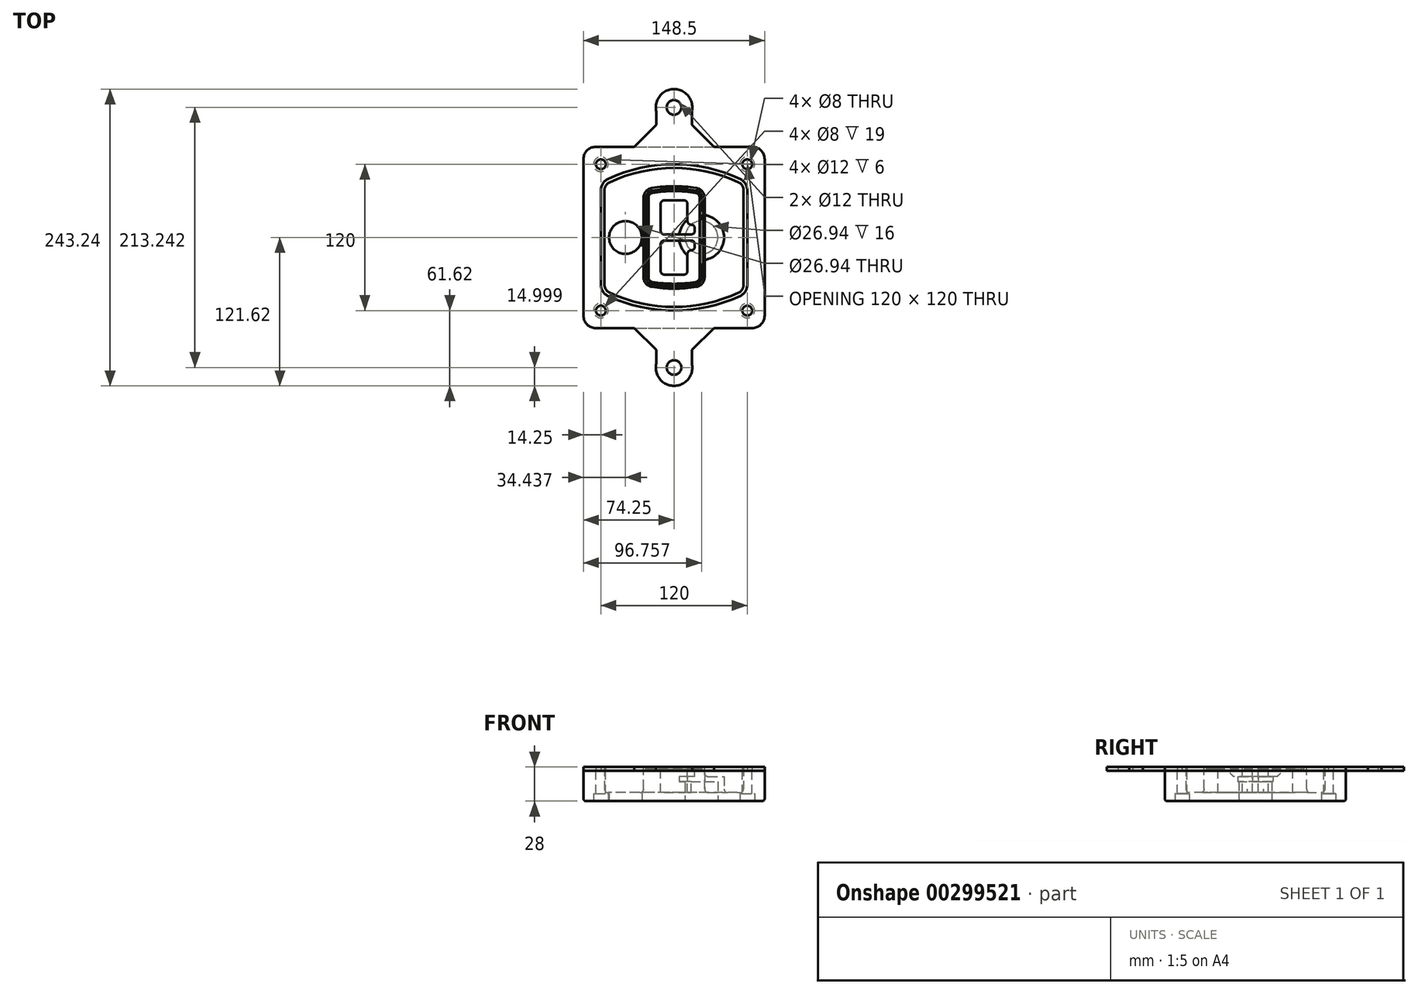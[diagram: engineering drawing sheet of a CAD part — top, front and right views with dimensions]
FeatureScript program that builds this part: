
annotation { "Feature Type Name" : "Feature", "Feature Type Description" : "" }
export const myFeature = defineFeature(function(context is Context, id is Id, definition is map)
    precondition{}
    {
        {
            var Q0;
            Q0=qCreatedBy(makeId("Top.planeOp"),FACE);
            var sketch = newSketch(context, id + "F0", { "sketchPlane" : qUnion([Q0])});
            skPoint(sketch, "E0.rect.middle", {"position": v(0, 0) * mm});
            skLineSegment(sketch, "E1.bottom", {"start": v(-64.25, -74.25) * mm, "end": v(64.25, -74.25) * mm});
            skLineSegment(sketch, "E1.top", {"start": v(-64.25, 74.25) * mm, "end": v(64.25, 74.25) * mm});
            skLineSegment(sketch, "E1.left", {"start": v(-74.25, -64.25) * mm, "end": v(-74.25, 64.25) * mm});
            skLineSegment(sketch, "E1.right", {"start": v(74.25, -64.25) * mm, "end": v(74.25, 64.25) * mm});
            skLineSegment(sketch, "E2", {"start": v(-74.25, 74.25) * mm, "end": v(74.25, -74.25) * mm, "construction": true});
            skLineSegment(sketch, "E3", {"start": v(74.25, 74.25) * mm, "end": v(-74.25, -74.25) * mm, "construction": true});
            skCircle(sketch, "E4", {"center": v(-60, 60) * mm, "radius": 4 * mm});
            skCircle(sketch, "E5", {"center": v(60, 60) * mm, "radius": 4 * mm});
            skCircle(sketch, "E6", {"center": v(60, -60) * mm, "radius": 4 * mm});
            skCircle(sketch, "E7", {"center": v(-60, -60) * mm, "radius": 4 * mm});
            skLineSegment(sketch, "E8", {"start": v(-60, 60) * mm, "end": v(60, 60) * mm, "construction": true});
            skLineSegment(sketch, "E9", {"start": v(60, 60) * mm, "end": v(60, -60) * mm, "construction": true});
            skLineSegment(sketch, "E10", {"start": v(60, -60) * mm, "end": v(-60, -60) * mm, "construction": true});
            skLineSegment(sketch, "E11", {"start": v(-60, -60) * mm, "end": v(-60, 60) * mm, "construction": true});
            skLineSegment(sketch, "E12", {"start": v(-60, 38.83) * mm, "end": v(-60, -38.83) * mm});
            skLineSegment(sketch, "E13", {"start": v(60, 38.83) * mm, "end": v(60, -38.83) * mm});
            skArc(sketch, "E14", {"start": v(54.26, 47.88) * mm, "mid": v(0, 60) * mm, "end": v(-54.26, 47.88) * mm});
            skArc(sketch, "E15", {"start": v(-54.26, -47.88) * mm, "mid": v(0, -60) * mm, "end": v(54.26, -47.88) * mm});
            skLineSegment(sketch, "E16", {"start": v(-60, 0) * mm, "end": v(60, 0) * mm, "construction": true});
            skPoint(sketch, "E17.visualSharp", {"position": v(-60, -45) * mm});
            skArc(sketch, "E17.filletArc", {"start": v(-60, -38.83) * mm, "mid": v(-58.44, -44.2) * mm, "end": v(-54.26, -47.88) * mm});
            skPoint(sketch, "E18.visualSharp", {"position": v(-60, 45) * mm});
            skArc(sketch, "E18.filletArc", {"start": v(-54.26, 47.88) * mm, "mid": v(-58.44, 44.2) * mm, "end": v(-60, 38.83) * mm});
            skPoint(sketch, "E19.visualSharp", {"position": v(60, 45) * mm});
            skArc(sketch, "E19.filletArc", {"start": v(60, 38.83) * mm, "mid": v(58.44, 44.2) * mm, "end": v(54.26, 47.88) * mm});
            skPoint(sketch, "E20.visualSharp", {"position": v(60, -45) * mm});
            skArc(sketch, "E20.filletArc", {"start": v(54.26, -47.88) * mm, "mid": v(58.44, -44.2) * mm, "end": v(60, -38.83) * mm});
            skPoint(sketch, "E21.visualSharp", {"position": v(-74.25, 74.25) * mm});
            skArc(sketch, "E21.filletArc", {"start": v(-64.25, 74.25) * mm, "mid": v(-71.32, 71.32) * mm, "end": v(-74.25, 64.25) * mm});
            skPoint(sketch, "E22.visualSharp", {"position": v(74.25, 74.25) * mm});
            skArc(sketch, "E22.filletArc", {"start": v(74.25, 64.25) * mm, "mid": v(71.32, 71.32) * mm, "end": v(64.25, 74.25) * mm});
            skPoint(sketch, "E23.visualSharp", {"position": v(74.25, -74.25) * mm});
            skArc(sketch, "E23.filletArc", {"start": v(64.25, -74.25) * mm, "mid": v(71.32, -71.32) * mm, "end": v(74.25, -64.25) * mm});
            skPoint(sketch, "E24.visualSharp", {"position": v(-74.25, -74.25) * mm});
            skArc(sketch, "E24.filletArc", {"start": v(-74.25, -64.25) * mm, "mid": v(-71.32, -71.32) * mm, "end": v(-64.25, -74.25) * mm});
            skArc(sketch, "E25.0", {"start": v(57, 38.83) * mm, "mid": v(55.9, 42.58) * mm, "end": v(52.98, 45.17) * mm});
            skLineSegment(sketch, "E25.1", {"start": v(57, 38.83) * mm, "end": v(57, -38.83) * mm});
            skArc(sketch, "E25.2", {"start": v(52.98, -45.17) * mm, "mid": v(55.9, -42.58) * mm, "end": v(57, -38.83) * mm});
            skArc(sketch, "E25.3", {"start": v(-52.98, -45.17) * mm, "mid": v(0, -57) * mm, "end": v(52.98, -45.17) * mm});
            skArc(sketch, "E25.4", {"start": v(-57, -38.83) * mm, "mid": v(-55.9, -42.58) * mm, "end": v(-52.98, -45.17) * mm});
            skArc(sketch, "E25.5", {"start": v(52.98, 45.17) * mm, "mid": v(0, 57) * mm, "end": v(-52.98, 45.17) * mm});
            skLineSegment(sketch, "E25.6", {"start": v(-57, 38.83) * mm, "end": v(-57, -38.83) * mm});
            skArc(sketch, "E25.7", {"start": v(-52.98, 45.17) * mm, "mid": v(-55.9, 42.58) * mm, "end": v(-57, 38.83) * mm});
            skArc(sketch, "E26.0", {"start": v(-55.96, 51.5) * mm, "mid": v(-61.82, 46.33) * mm, "end": v(-64, 38.83) * mm});
            skArc(sketch, "E26.1", {"start": v(55.96, 51.5) * mm, "mid": v(0, 64) * mm, "end": v(-55.96, 51.5) * mm});
            skArc(sketch, "E26.2", {"start": v(64, 38.83) * mm, "mid": v(61.82, 46.33) * mm, "end": v(55.96, 51.5) * mm});
            skLineSegment(sketch, "E26.3", {"start": v(64, 38.83) * mm, "end": v(64, -38.83) * mm});
            skArc(sketch, "E26.4", {"start": v(55.96, -51.5) * mm, "mid": v(61.82, -46.33) * mm, "end": v(64, -38.83) * mm});
            skLineSegment(sketch, "E26.5", {"start": v(-64, 38.83) * mm, "end": v(-64, -38.83) * mm});
            skArc(sketch, "E26.6", {"start": v(-55.96, -51.5) * mm, "mid": v(0, -64) * mm, "end": v(55.96, -51.5) * mm});
            skArc(sketch, "E26.7", {"start": v(-64, -38.83) * mm, "mid": v(-61.82, -46.33) * mm, "end": v(-55.96, -51.5) * mm});
            skSolve(sketch);
        }
        {
            var Q0;
            Q0=makeQuery(id+"F0.imprint","IMPRINT",FACE,{"disambiguationData":[TD([[makeQuery(id+"F0.imprint","IMPRINT",EDGE,{"derivedFrom":sQuery(id+"F0.wireOp",EDGE,"E1.bottom")}),1.0]])]});
            var Q1;
            Q1=makeQuery(id+"F0.imprint","IMPRINT",FACE,{"disambiguationData":[TD([[makeQuery(id+"F0.imprint","IMPRINT",EDGE,{"derivedFrom":sQuery(id+"F0.wireOp",EDGE,"E12")}),1.0]])]});
            var Q2;
            Q2=makeQuery(id+"F0.imprint","IMPRINT",FACE,{"disambiguationData":[TD([[makeQuery(id+"F0.imprint","IMPRINT",EDGE,{"derivedFrom":sQuery(id+"F0.wireOp",EDGE,"E25.0")}),1.0]])]});
            var Q3;
            Q3=makeQuery(id+"F0.imprint","IMPRINT",FACE,{"disambiguationData":[TD([[makeQuery(id+"F0.imprint","IMPRINT",EDGE,{"derivedFrom":sQuery(id+"F0.wireOp",EDGE,"E12")}),-1.0]])]});
            extrude(context, id + "F1", {"entities" : qUnion([Q0, Q1, Q2, Q3]), "oppositeDirection" : true, "depth" : 25 * mm});
        }
        {
            var Q0;
            Q0=makeQuery(id+"F0.imprint","IMPRINT",FACE,{"disambiguationData":[TD([[makeQuery(id+"F0.imprint","IMPRINT",EDGE,{"derivedFrom":sQuery(id+"F0.wireOp",EDGE,"E12")}),1.0]])]});
            extrude(context, id + "F2", {"entities" : qUnion([Q0]), "operationType" : NewBodyOperationType.ADD, "depth" : 3 * mm});
        }
        {
            var Q0;
            Q0=makeQuery(id+"F0.imprint","IMPRINT",FACE,{"disambiguationData":[TD([[makeQuery(id+"F0.imprint","IMPRINT",EDGE,{"derivedFrom":sQuery(id+"F0.wireOp",EDGE,"E25.0")}),1.0]])]});
            extrude(context, id + "F3", {"entities" : qUnion([Q0]), "operationType" : NewBodyOperationType.REMOVE, "oppositeDirection" : true, "depth" : 18 * mm});
        }
        {
            var Q0;
            Q0=makeQuery(id+"F2.opExtrude","CAP_FACE",FACE,{"disambiguationData":[OSD([sQuery(id+"F0.wireOp",EDGE,"E12"),sQuery(id+"F0.wireOp",EDGE,"E13"),sQuery(id+"F0.wireOp",EDGE,"E14"),sQuery(id+"F0.wireOp",EDGE,"E15"),sQuery(id+"F0.wireOp",EDGE,"E17.filletArc"),sQuery(id+"F0.wireOp",EDGE,"E18.filletArc"),sQuery(id+"F0.wireOp",EDGE,"E19.filletArc"),sQuery(id+"F0.wireOp",EDGE,"E20.filletArc"),sQuery(id+"F0.wireOp",EDGE,"E25.0"),sQuery(id+"F0.wireOp",EDGE,"E25.1"),sQuery(id+"F0.wireOp",EDGE,"E25.2"),sQuery(id+"F0.wireOp",EDGE,"E25.3"),sQuery(id+"F0.wireOp",EDGE,"E25.4"),sQuery(id+"F0.wireOp",EDGE,"E25.5"),sQuery(id+"F0.wireOp",EDGE,"E25.6"),sQuery(id+"F0.wireOp",EDGE,"E25.7")])],"isStart":false});
            var sketch = newSketch(context, id + "F4", { "sketchPlane" : qUnion([Q0])});
            skArc(sketch, "E27.0", {"start": v(-18.34, -40.45) * mm, "mid": v(0, -42) * mm, "end": v(18.34, -40.45) * mm});
            skArc(sketch, "E28.0", {"start": v(18.34, 40.45) * mm, "mid": v(0, 42) * mm, "end": v(-18.34, 40.45) * mm});
            skLineSegment(sketch, "E29", {"start": v(-25, 32.57) * mm, "end": v(-25, -32.57) * mm});
            skLineSegment(sketch, "E30", {"start": v(25, 32.57) * mm, "end": v(25, -32.57) * mm});
            skLineSegment(sketch, "E31", {"start": v(-25, 39.1) * mm, "end": v(25, 39.1) * mm, "construction": true});
            skLineSegment(sketch, "E32", {"start": v(-25, -39.1) * mm, "end": v(25, -39.1) * mm, "construction": true});
            skPoint(sketch, "E33.visualSharp", {"position": v(-25, 39.1) * mm});
            skArc(sketch, "E33.filletArc", {"start": v(-18.34, 40.45) * mm, "mid": v(-23.11, 37.73) * mm, "end": v(-25, 32.57) * mm});
            skPoint(sketch, "E34.visualSharp", {"position": v(25, 39.1) * mm});
            skArc(sketch, "E34.filletArc", {"start": v(25, 32.57) * mm, "mid": v(23.11, 37.73) * mm, "end": v(18.34, 40.45) * mm});
            skPoint(sketch, "E35.visualSharp", {"position": v(25, -39.1) * mm});
            skArc(sketch, "E35.filletArc", {"start": v(18.34, -40.45) * mm, "mid": v(23.11, -37.73) * mm, "end": v(25, -32.57) * mm});
            skPoint(sketch, "E36.visualSharp", {"position": v(-25, -39.1) * mm});
            skArc(sketch, "E36.filletArc", {"start": v(-25, -32.57) * mm, "mid": v(-23.11, -37.73) * mm, "end": v(-18.34, -40.45) * mm});
            skArc(sketch, "E37.0", {"start": v(52.98, 45.17) * mm, "mid": v(0, 57) * mm, "end": v(-52.98, 45.17) * mm});
            skArc(sketch, "E37.1", {"start": v(-52.98, 45.17) * mm, "mid": v(-55.9, 42.58) * mm, "end": v(-57, 38.83) * mm});
            skLineSegment(sketch, "E37.2", {"start": v(-57, 38.83) * mm, "end": v(-57, -38.83) * mm});
            skArc(sketch, "E37.3", {"start": v(-57, -38.83) * mm, "mid": v(-55.9, -42.58) * mm, "end": v(-52.98, -45.17) * mm});
            skArc(sketch, "E37.4", {"start": v(-52.98, -45.17) * mm, "mid": v(0, -57) * mm, "end": v(52.98, -45.17) * mm});
            skArc(sketch, "E37.5", {"start": v(52.98, -45.17) * mm, "mid": v(55.9, -42.58) * mm, "end": v(57, -38.83) * mm});
            skLineSegment(sketch, "E37.6", {"start": v(57, 38.83) * mm, "end": v(57, -38.83) * mm});
            skArc(sketch, "E37.7", {"start": v(57, 38.83) * mm, "mid": v(55.9, 42.58) * mm, "end": v(52.98, 45.17) * mm});
            skLineSegment(sketch, "E38.0", {"start": v(23, 32.57) * mm, "end": v(23, -32.57) * mm});
            skArc(sketch, "E38.1", {"start": v(18, -38.48) * mm, "mid": v(21.58, -36.44) * mm, "end": v(23, -32.57) * mm});
            skArc(sketch, "E38.2", {"start": v(-18, -38.48) * mm, "mid": v(0, -40) * mm, "end": v(18, -38.48) * mm});
            skArc(sketch, "E38.3", {"start": v(-23, -32.57) * mm, "mid": v(-21.58, -36.44) * mm, "end": v(-18, -38.48) * mm});
            skLineSegment(sketch, "E38.4", {"start": v(-23, 32.57) * mm, "end": v(-23, -32.57) * mm});
            skArc(sketch, "E38.5", {"start": v(23, 32.57) * mm, "mid": v(21.58, 36.44) * mm, "end": v(18, 38.48) * mm});
            skArc(sketch, "E38.6", {"start": v(-18, 38.48) * mm, "mid": v(-21.58, 36.44) * mm, "end": v(-23, 32.57) * mm});
            skArc(sketch, "E38.7", {"start": v(18, 38.48) * mm, "mid": v(0, 40) * mm, "end": v(-18, 38.48) * mm});
            skArc(sketch, "E39.0", {"start": v(21, 32.57) * mm, "mid": v(20.06, 35.15) * mm, "end": v(17.67, 36.5) * mm});
            skLineSegment(sketch, "E39.1", {"start": v(21, 32.57) * mm, "end": v(21, -32.57) * mm});
            skArc(sketch, "E39.2", {"start": v(17.67, -36.5) * mm, "mid": v(20.06, -35.15) * mm, "end": v(21, -32.57) * mm});
            skArc(sketch, "E39.3", {"start": v(-17.67, -36.5) * mm, "mid": v(0, -38) * mm, "end": v(17.67, -36.5) * mm});
            skArc(sketch, "E39.4", {"start": v(-21, -32.57) * mm, "mid": v(-20.06, -35.15) * mm, "end": v(-17.67, -36.5) * mm});
            skArc(sketch, "E39.5", {"start": v(17.67, 36.5) * mm, "mid": v(0, 38) * mm, "end": v(-17.67, 36.5) * mm});
            skLineSegment(sketch, "E39.6", {"start": v(-21, 32.57) * mm, "end": v(-21, -32.57) * mm});
            skArc(sketch, "E39.7", {"start": v(-17.67, 36.5) * mm, "mid": v(-20.06, 35.15) * mm, "end": v(-21, 32.57) * mm});
            skLineSegment(sketch, "E40", {"start": v(-25, 0) * mm, "end": v(25, 0) * mm, "construction": true});
            skLineSegment(sketch, "E41", {"start": v(-11, 5.5) * mm, "end": v(-11, 27.5) * mm});
            skLineSegment(sketch, "E42", {"start": v(-8, 30.5) * mm, "end": v(8, 30.5) * mm});
            skLineSegment(sketch, "E43", {"start": v(11, 27.5) * mm, "end": v(11, 13.5) * mm});
            skLineSegment(sketch, "E44", {"start": v(14, 10.5) * mm, "end": v(14, 10.5) * mm});
            skLineSegment(sketch, "E45", {"start": v(17, 7.5) * mm, "end": v(17, 5.5) * mm});
            skLineSegment(sketch, "E46", {"start": v(14, 2.5) * mm, "end": v(-8, 2.5) * mm});
            skPoint(sketch, "E47.visualSharp", {"position": v(-11, 30.5) * mm});
            skArc(sketch, "E47.filletArc", {"start": v(-8, 30.5) * mm, "mid": v(-10.12, 29.62) * mm, "end": v(-11, 27.5) * mm});
            skPoint(sketch, "E48.visualSharp", {"position": v(11, 30.5) * mm});
            skArc(sketch, "E48.filletArc", {"start": v(11, 27.5) * mm, "mid": v(10.12, 29.62) * mm, "end": v(8, 30.5) * mm});
            skPoint(sketch, "E49.visualSharp", {"position": v(11, 10.5) * mm});
            skArc(sketch, "E49.filletArc", {"start": v(11, 13.5) * mm, "mid": v(11.88, 11.38) * mm, "end": v(14, 10.5) * mm});
            skPoint(sketch, "E50.visualSharp", {"position": v(17, 10.5) * mm});
            skArc(sketch, "E50.filletArc", {"start": v(17, 7.5) * mm, "mid": v(16.12, 9.62) * mm, "end": v(14, 10.5) * mm});
            skPoint(sketch, "E51.visualSharp", {"position": v(17, 2.5) * mm});
            skArc(sketch, "E51.filletArc", {"start": v(14, 2.5) * mm, "mid": v(16.12, 3.38) * mm, "end": v(17, 5.5) * mm});
            skPoint(sketch, "E52.visualSharp", {"position": v(-11, 2.5) * mm});
            skArc(sketch, "E52.filletArc", {"start": v(-11, 5.5) * mm, "mid": v(-10.12, 3.38) * mm, "end": v(-8, 2.5) * mm});
            skLineSegment(sketch, "E53.0.MirrorCS", {"start": v(14, -2.5) * mm, "end": v(-8, -2.5) * mm});
            skArc(sketch, "E54.0.MirrorCS", {"start": v(-11, -5.5) * mm, "mid": v(-10.12, -3.38) * mm, "end": v(-8, -2.5) * mm});
            skLineSegment(sketch, "E55.0.MirrorCS", {"start": v(-11, -5.5) * mm, "end": v(-11, -27.5) * mm});
            skArc(sketch, "E56.0.MirrorCS", {"start": v(-8, -30.5) * mm, "mid": v(-10.12, -29.62) * mm, "end": v(-11, -27.5) * mm});
            skLineSegment(sketch, "E57.0.MirrorCS", {"start": v(-8, -30.5) * mm, "end": v(8, -30.5) * mm});
            skArc(sketch, "E58.0.MirrorCS", {"start": v(11, -27.5) * mm, "mid": v(10.12, -29.62) * mm, "end": v(8, -30.5) * mm});
            skLineSegment(sketch, "E59.0.MirrorCS", {"start": v(11, -27.5) * mm, "end": v(11, -13.5) * mm});
            skArc(sketch, "E60.0.MirrorCS", {"start": v(11, -13.5) * mm, "mid": v(11.88, -11.38) * mm, "end": v(14, -10.5) * mm});
            skArc(sketch, "E61.0.MirrorCS", {"start": v(17, -7.5) * mm, "mid": v(16.12, -9.62) * mm, "end": v(14, -10.5) * mm});
            skLineSegment(sketch, "E62.0.MirrorCS", {"start": v(17, -7.5) * mm, "end": v(17, -5.5) * mm});
            skArc(sketch, "E63.0.MirrorCS", {"start": v(14, -2.5) * mm, "mid": v(16.12, -3.38) * mm, "end": v(17, -5.5) * mm});
            skSolve(sketch);
        }
        {
            var Q0;
            Q0=makeQuery(id+"F4.imprint","IMPRINT",FACE,{"disambiguationData":[TD([[makeQuery(id+"F4.imprint","IMPRINT",EDGE,{"derivedFrom":sQuery(id+"F4.wireOp",EDGE,"E27.0")}),1.0]])]});
            var Q1;
            Q1=makeQuery(id+"F4.imprint","IMPRINT",FACE,{"disambiguationData":[TD([[makeQuery(id+"F4.imprint","IMPRINT",EDGE,{"derivedFrom":sQuery(id+"F4.wireOp",EDGE,"E38.0")}),-1.0]])]});
            var Q2;
            Q2=makeQuery(id+"F4.imprint","IMPRINT",FACE,{"disambiguationData":[TD([[makeQuery(id+"F4.imprint","IMPRINT",EDGE,{"derivedFrom":sQuery(id+"F4.wireOp",EDGE,"E39.0")}),1.0]])]});
            extrude(context, id + "F5", {"entities" : qUnion([Q0, Q1, Q2]), "operationType" : NewBodyOperationType.ADD, "endBound" : BoundingType.UP_TO_NEXT, "oppositeDirection" : true, "depth" : 25 * mm});
        }
        {
            var Q0;
            Q0=makeQuery(id+"F4.imprint","IMPRINT",FACE,{"disambiguationData":[TD([[makeQuery(id+"F4.imprint","IMPRINT",EDGE,{"derivedFrom":sQuery(id+"F4.wireOp",EDGE,"E38.0")}),-1.0]])]});
            extrude(context, id + "F6", {"entities" : qUnion([Q0]), "operationType" : NewBodyOperationType.REMOVE, "oppositeDirection" : true, "depth" : 2 * mm});
        }
        {
            var Q0;
            Q0=makeQuery(id+"F1.opExtrude","CAP_FACE",FACE,{"disambiguationData":[OSD([sQuery(id+"F0.wireOp",EDGE,"E1.bottom"),sQuery(id+"F0.wireOp",EDGE,"E1.top"),sQuery(id+"F0.wireOp",EDGE,"E1.left"),sQuery(id+"F0.wireOp",EDGE,"E1.right"),sQuery(id+"F0.wireOp",EDGE,"E4"),sQuery(id+"F0.wireOp",EDGE,"E5"),sQuery(id+"F0.wireOp",EDGE,"E6"),sQuery(id+"F0.wireOp",EDGE,"E7"),sQuery(id+"F0.wireOp",EDGE,"E21.filletArc"),sQuery(id+"F0.wireOp",EDGE,"E22.filletArc"),sQuery(id+"F0.wireOp",EDGE,"E23.filletArc"),sQuery(id+"F0.wireOp",EDGE,"E24.filletArc")])],"isStart":false});
            var sketch = newSketch(context, id + "F7", { "sketchPlane" : qUnion([Q0])});
            skCircle(sketch, "E64", {"center": v(22.5, 0) * mm, "radius": 13.47 * mm});
            skCircle(sketch, "E65", {"center": v(-39.81, 0) * mm, "radius": 13.47 * mm});
            skLineSegment(sketch, "E66", {"start": v(74.25, 0) * mm, "end": v(-74.25, 0) * mm});
            skCircle(sketch, "E67", {"center": v(22.5, 0) * mm, "radius": 18.47 * mm});
            skCircle(sketch, "E68", {"center": v(60, -60) * mm, "radius": 6 * mm});
            skCircle(sketch, "E69", {"center": v(-60, -60) * mm, "radius": 6 * mm});
            skCircle(sketch, "E70", {"center": v(-60, 60) * mm, "radius": 6 * mm});
            skCircle(sketch, "E71", {"center": v(60, 60) * mm, "radius": 6 * mm});
            skSolve(sketch);
        }
        {
            var Q0;
            {var subQ1=sQuery(id+"F7.wireOp",EDGE,"E66");var subQ4=sQuery(id+"F7.wireOp",EDGE,"E64");var subQ6=makeQuery(id+"F7.imprint","INTERSECT",VERTEX,{"disambiguationData":[OD(0.0)],"derivedFrom":[subQ4,subQ1]});Q0=makeQuery(id+"F7.imprint","IMPRINT",FACE,{"disambiguationData":[TD([[makeQuery(id+"F7.imprint","IMPRINT",EDGE,{"disambiguationData":[TD([[subQ6,-1.0]])],"derivedFrom":subQ4}),-1.0]])]});}
            var Q1;
            {var subQ0=sQuery(id+"F7.wireOp",EDGE,"E66");var subQ1=sQuery(id+"F7.wireOp",EDGE,"E64");var subQ3=makeQuery(id+"F7.imprint","INTERSECT",VERTEX,{"disambiguationData":[OD(0.0)],"derivedFrom":[subQ1,subQ0]});Q1=makeQuery(id+"F7.imprint","IMPRINT",FACE,{"disambiguationData":[TD([[makeQuery(id+"F7.imprint","IMPRINT",EDGE,{"disambiguationData":[TD([[subQ3,-1.0]])],"derivedFrom":subQ1}),1.0]])]});}
            var Q2;
            {var subQ0=sQuery(id+"F7.wireOp",EDGE,"E66");var subQ1=sQuery(id+"F7.wireOp",EDGE,"E64");var subQ3=makeQuery(id+"F7.imprint","INTERSECT",VERTEX,{"disambiguationData":[OD(0.0)],"derivedFrom":[subQ1,subQ0]});Q2=makeQuery(id+"F7.imprint","IMPRINT",FACE,{"disambiguationData":[TD([[makeQuery(id+"F7.imprint","IMPRINT",EDGE,{"disambiguationData":[TD([[subQ3,1.0]])],"derivedFrom":subQ1}),1.0]])]});}
            var Q3;
            {var subQ1=sQuery(id+"F7.wireOp",EDGE,"E66");var subQ4=sQuery(id+"F7.wireOp",EDGE,"E64");var subQ6=makeQuery(id+"F7.imprint","INTERSECT",VERTEX,{"disambiguationData":[OD(0.0)],"derivedFrom":[subQ4,subQ1]});Q3=makeQuery(id+"F7.imprint","IMPRINT",FACE,{"disambiguationData":[TD([[makeQuery(id+"F7.imprint","IMPRINT",EDGE,{"disambiguationData":[TD([[subQ6,1.0]])],"derivedFrom":subQ4}),-1.0]])]});}
            extrude(context, id + "F8", {"entities" : qUnion([Q0, Q1, Q2, Q3]), "operationType" : NewBodyOperationType.ADD, "oppositeDirection" : true, "depth" : 20 * mm});
        }
        {
            var Q0;
            {var subQ0=sQuery(id+"F7.wireOp",EDGE,"E66");var subQ1=sQuery(id+"F7.wireOp",EDGE,"E64");var subQ3=makeQuery(id+"F7.imprint","INTERSECT",VERTEX,{"disambiguationData":[OD(0.0)],"derivedFrom":[subQ1,subQ0]});Q0=makeQuery(id+"F7.imprint","IMPRINT",FACE,{"disambiguationData":[TD([[makeQuery(id+"F7.imprint","IMPRINT",EDGE,{"disambiguationData":[TD([[subQ3,-1.0]])],"derivedFrom":subQ1}),1.0]])]});}
            var Q1;
            {var subQ0=sQuery(id+"F7.wireOp",EDGE,"E66");var subQ1=sQuery(id+"F7.wireOp",EDGE,"E64");var subQ3=makeQuery(id+"F7.imprint","INTERSECT",VERTEX,{"disambiguationData":[OD(0.0)],"derivedFrom":[subQ1,subQ0]});Q1=makeQuery(id+"F7.imprint","IMPRINT",FACE,{"disambiguationData":[TD([[makeQuery(id+"F7.imprint","IMPRINT",EDGE,{"disambiguationData":[TD([[subQ3,1.0]])],"derivedFrom":subQ1}),1.0]])]});}
            extrude(context, id + "F9", {"entities" : qUnion([Q0, Q1]), "operationType" : NewBodyOperationType.REMOVE, "oppositeDirection" : true, "depth" : 16 * mm});
        }
        {
            var Q0;
            {var subQ0=sQuery(id+"F7.wireOp",EDGE,"E66");var subQ1=sQuery(id+"F7.wireOp",EDGE,"E65");var subQ3=makeQuery(id+"F7.imprint","INTERSECT",VERTEX,{"disambiguationData":[OD(0.0)],"derivedFrom":[subQ1,subQ0]});Q0=makeQuery(id+"F7.imprint","IMPRINT",FACE,{"disambiguationData":[TD([[makeQuery(id+"F7.imprint","IMPRINT",EDGE,{"disambiguationData":[TD([[subQ3,-1.0]])],"derivedFrom":subQ1}),1.0]])]});}
            var Q1;
            {var subQ0=sQuery(id+"F7.wireOp",EDGE,"E66");var subQ1=sQuery(id+"F7.wireOp",EDGE,"E65");var subQ3=makeQuery(id+"F7.imprint","INTERSECT",VERTEX,{"disambiguationData":[OD(0.0)],"derivedFrom":[subQ1,subQ0]});Q1=makeQuery(id+"F7.imprint","IMPRINT",FACE,{"disambiguationData":[TD([[makeQuery(id+"F7.imprint","IMPRINT",EDGE,{"disambiguationData":[TD([[subQ3,1.0]])],"derivedFrom":subQ1}),1.0]])]});}
            extrude(context, id + "F10", {"entities" : qUnion([Q0, Q1]), "operationType" : NewBodyOperationType.REMOVE, "oppositeDirection" : true, "depth" : 25 * mm});
        }
        {
            var Q0;
            Q0=makeQuery(id+"F7.imprint","IMPRINT",FACE,{"disambiguationData":[TD([[makeQuery(id+"F7.imprint","IMPRINT",EDGE,{"derivedFrom":sQuery(id+"F7.wireOp",EDGE,"E68")}),1.0]])]});
            var Q1;
            Q1=makeQuery(id+"F7.imprint","IMPRINT",FACE,{"disambiguationData":[TD([[makeQuery(id+"F7.imprint","IMPRINT",EDGE,{"derivedFrom":makeQuery(id+"F1.opExtrude","CAP_EDGE",EDGE,{"disambiguationData":[OSD([sQuery(id+"F0.wireOp",EDGE,"E5")])],"isStart":false})}),-1.0]])]});
            var Q2;
            Q2=makeQuery(id+"F7.imprint","IMPRINT",FACE,{"disambiguationData":[TD([[makeQuery(id+"F7.imprint","IMPRINT",EDGE,{"derivedFrom":sQuery(id+"F7.wireOp",EDGE,"E69")}),1.0]])]});
            var Q3;
            Q3=makeQuery(id+"F7.imprint","IMPRINT",FACE,{"disambiguationData":[TD([[makeQuery(id+"F7.imprint","IMPRINT",EDGE,{"derivedFrom":makeQuery(id+"F1.opExtrude","CAP_EDGE",EDGE,{"disambiguationData":[OSD([sQuery(id+"F0.wireOp",EDGE,"E4")])],"isStart":false})}),-1.0]])]});
            var Q4;
            Q4=makeQuery(id+"F7.imprint","IMPRINT",FACE,{"disambiguationData":[TD([[makeQuery(id+"F7.imprint","IMPRINT",EDGE,{"derivedFrom":sQuery(id+"F7.wireOp",EDGE,"E70")}),1.0]])]});
            var Q5;
            Q5=makeQuery(id+"F7.imprint","IMPRINT",FACE,{"disambiguationData":[TD([[makeQuery(id+"F7.imprint","IMPRINT",EDGE,{"derivedFrom":makeQuery(id+"F1.opExtrude","CAP_EDGE",EDGE,{"disambiguationData":[OSD([sQuery(id+"F0.wireOp",EDGE,"E7")])],"isStart":false})}),-1.0]])]});
            var Q6;
            Q6=makeQuery(id+"F7.imprint","IMPRINT",FACE,{"disambiguationData":[TD([[makeQuery(id+"F7.imprint","IMPRINT",EDGE,{"derivedFrom":sQuery(id+"F7.wireOp",EDGE,"E71")}),1.0]])]});
            var Q7;
            Q7=makeQuery(id+"F7.imprint","IMPRINT",FACE,{"disambiguationData":[TD([[makeQuery(id+"F7.imprint","IMPRINT",EDGE,{"derivedFrom":makeQuery(id+"F1.opExtrude","CAP_EDGE",EDGE,{"disambiguationData":[OSD([sQuery(id+"F0.wireOp",EDGE,"E6")])],"isStart":false})}),-1.0]])]});
            extrude(context, id + "F11", {"entities" : qUnion([Q0, Q1, Q2, Q3, Q4, Q5, Q6, Q7]), "operationType" : NewBodyOperationType.REMOVE, "oppositeDirection" : true, "depth" : 6 * mm});
        }
        {
            var Q0;
            Q0=makeQuery(id+"F9.boolean.opBoolean","COPY",FACE,{"derivedFrom":makeQuery(id+"F9.opExtrude","CAP_FACE",FACE,{"disambiguationData":[OSD([sQuery(id+"F7.wireOp",EDGE,"E64")])],"isStart":false})});
            var sketch = newSketch(context, id + "F12", { "sketchPlane" : qUnion([Q0])});
            skArc(sketch, "E72.0", {"start": v(11, 14.45) * mm, "mid": v(6.45, 9.13) * mm, "end": v(4.2, 2.5) * mm});
            skArc(sketch, "E72.1", {"start": v(4.2, -2.5) * mm, "mid": v(6.45, -9.13) * mm, "end": v(11, -14.45) * mm});
            skLineSegment(sketch, "E73", {"start": v(4.2, -2.5) * mm, "end": v(14, -2.5) * mm});
            skLineSegment(sketch, "E74.0", {"start": v(14, 2.5) * mm, "end": v(4.2, 2.5) * mm});
            skArc(sketch, "E74.1", {"start": v(14, 2.5) * mm, "mid": v(16.12, 3.38) * mm, "end": v(17, 5.5) * mm});
            skLineSegment(sketch, "E74.2", {"start": v(17, 7.5) * mm, "end": v(17, 5.5) * mm});
            skArc(sketch, "E74.3", {"start": v(17, 7.5) * mm, "mid": v(16.12, 9.62) * mm, "end": v(14, 10.5) * mm});
            skArc(sketch, "E74.4", {"start": v(11, 13.5) * mm, "mid": v(11.88, 11.38) * mm, "end": v(14, 10.5) * mm});
            skLineSegment(sketch, "E74.5", {"start": v(11, 14.45) * mm, "end": v(11, 13.5) * mm});
            skLineSegment(sketch, "E74.7", {"start": v(14, -2.5) * mm, "end": v(4.2, -2.5) * mm});
            skArc(sketch, "E74.8", {"start": v(14, -2.5) * mm, "mid": v(16.12, -3.38) * mm, "end": v(17, -5.5) * mm});
            skLineSegment(sketch, "E74.9", {"start": v(17, -7.5) * mm, "end": v(17, -5.5) * mm});
            skArc(sketch, "E74.10", {"start": v(17, -7.5) * mm, "mid": v(16.12, -9.62) * mm, "end": v(14, -10.5) * mm});
            skArc(sketch, "E74.11", {"start": v(11, -13.5) * mm, "mid": v(11.88, -11.38) * mm, "end": v(14, -10.5) * mm});
            skLineSegment(sketch, "E74.12", {"start": v(11, -14.45) * mm, "end": v(11, -13.5) * mm});
            skPoint(sketch, "E75.orphan", {"position": v(11, -27.5) * mm});
            skPoint(sketch, "E76.orphan", {"position": v(-8, -2.5) * mm});
            skPoint(sketch, "E77.orphan", {"position": v(-8, 2.5) * mm});
            skPoint(sketch, "E78.orphan", {"position": v(11, 27.5) * mm});
            skSolve(sketch);
        }
        {
            var Q0;
            {var subQ7=sQuery(id+"F12.wireOp",EDGE,"E72.0");var subQ14=sQuery(id+"F12.wireOp",EDGE,"E72.1");var subQ16=sQuery(id+"F12.wireOp",EDGE,"E74.1");var subQ18=sQuery(id+"F12.wireOp",EDGE,"E74.8");Q0=qUnion([makeQuery(id+"F12.imprint","IMPRINT",FACE,{"disambiguationData":[TD([[makeQuery(id+"F12.imprint","IMPRINT",EDGE,{"derivedFrom":subQ7}),1.0]])]}),makeQuery(id+"F12.imprint","IMPRINT",FACE,{"disambiguationData":[TD([[makeQuery(id+"F12.imprint","IMPRINT",EDGE,{"derivedFrom":subQ14}),1.0]])]}),makeQuery(id+"F12.imprint","IMPRINT",FACE,{"disambiguationData":[TD([[makeQuery(id+"F12.imprint","IMPRINT",EDGE,{"derivedFrom":subQ16}),1.0]])]}),makeQuery(id+"F12.imprint","IMPRINT",FACE,{"disambiguationData":[TD([[makeQuery(id+"F12.imprint","IMPRINT",EDGE,{"derivedFrom":subQ18}),-1.0]])]})]);}
            var Q1;
            Q1=makeQuery(id+"F5.boolean.opBoolean","SPLIT",FACE,{"disambiguationData":[TD([makeQuery(id+"F5.opExtrude","SWEPT_FACE",FACE,{"disambiguationData":[OSD([sQuery(id+"F4.wireOp",EDGE,"E41")])]})])],"derivedFrom":makeQuery(id+"F3.boolean.opBoolean","COPY",FACE,{"derivedFrom":makeQuery(id+"F3.opExtrude","CAP_FACE",FACE,{"disambiguationData":[OSD([sQuery(id+"F0.wireOp",EDGE,"E25.0"),sQuery(id+"F0.wireOp",EDGE,"E25.1"),sQuery(id+"F0.wireOp",EDGE,"E25.2"),sQuery(id+"F0.wireOp",EDGE,"E25.3"),sQuery(id+"F0.wireOp",EDGE,"E25.4"),sQuery(id+"F0.wireOp",EDGE,"E25.5"),sQuery(id+"F0.wireOp",EDGE,"E25.6"),sQuery(id+"F0.wireOp",EDGE,"E25.7")])],"isStart":false})})});
            extrude(context, id + "F13", {"entities" : qUnion([Q0]), "operationType" : NewBodyOperationType.REMOVE, "endBound" : BoundingType.UP_TO_SURFACE, "endBoundEntityFace" : qUnion([Q1]), "depth" : 25 * mm});
        }
        {
            var Q0;
            Q0=makeQuery(id+"F3.boolean.opBoolean","COPY",EDGE,{"derivedFrom":makeQuery(id+"F3.opExtrude","CAP_EDGE",EDGE,{"disambiguationData":[OSD([sQuery(id+"F0.wireOp",EDGE,"E25.6")])],"isStart":false})});
            var Q1;
            Q1=makeQuery(id+"F8.boolean.opBoolean","INTERSECT",EDGE,{"derivedFrom":[makeQuery(id+"F5.opExtrude","SWEPT_FACE",FACE,{"disambiguationData":[OSD([sQuery(id+"F4.wireOp",EDGE,"E30")])]}),makeQuery(id+"F8.opExtrude","CAP_FACE",FACE,{"disambiguationData":[OSD([sQuery(id+"F7.wireOp",EDGE,"E67")])],"isStart":false})]});
            var Q2;
            Q2=makeQuery(id+"F8.boolean.opBoolean","INTERSECT",EDGE,{"disambiguationData":[OD(1.0)],"derivedFrom":[makeQuery(id+"F5.opExtrude","SWEPT_FACE",FACE,{"disambiguationData":[OSD([sQuery(id+"F4.wireOp",EDGE,"E30")])]}),makeQuery(id+"F8.opExtrude","SWEPT_FACE",FACE,{"disambiguationData":[OSD([sQuery(id+"F7.wireOp",EDGE,"E67")])]})]});
            var Q3;
            {var subQ0=sQuery(id+"F4.wireOp",EDGE,"E30");Q3=makeQuery(id+"F8.boolean.opBoolean","SPLIT",EDGE,{"disambiguationData":[TD([makeQuery(id+"F5.opExtrude","SWEPT_FACE",FACE,{"disambiguationData":[OSD([sQuery(id+"F4.wireOp",EDGE,"E35.filletArc")])]})])],"derivedFrom":makeQuery(id+"F5.opExtrude","CAP_EDGE",EDGE,{"disambiguationData":[OSD([subQ0])],"isStart":false})});}
            var Q4;
            {var subQ0=sQuery(id+"F0.wireOp",EDGE,"E25.7");var subQ1=sQuery(id+"F0.wireOp",EDGE,"E25.1");var subQ2=sQuery(id+"F0.wireOp",EDGE,"E25.6");var subQ3=sQuery(id+"F0.wireOp",EDGE,"E25.5");var subQ4=sQuery(id+"F0.wireOp",EDGE,"E25.4");var subQ5=sQuery(id+"F0.wireOp",EDGE,"E25.0");var subQ6=sQuery(id+"F0.wireOp",EDGE,"E25.2");var subQ7=sQuery(id+"F0.wireOp",EDGE,"E25.3");Q4=makeQuery(id+"F8.boolean.opBoolean","INTERSECT",EDGE,{"derivedFrom":[makeQuery(id+"F5.boolean.opBoolean","SPLIT",FACE,{"disambiguationData":[TD([makeQuery(id+"F2.opExtrude","SWEPT_FACE",FACE,{"disambiguationData":[OSD([subQ5])]})])],"derivedFrom":makeQuery(id+"F3.boolean.opBoolean","COPY",FACE,{"derivedFrom":makeQuery(id+"F3.opExtrude","CAP_FACE",FACE,{"disambiguationData":[OSD([subQ5,subQ1,subQ6,subQ7,subQ4,subQ3,subQ2,subQ0])],"isStart":false})})}),makeQuery(id+"F8.opExtrude","SWEPT_FACE",FACE,{"disambiguationData":[OSD([sQuery(id+"F7.wireOp",EDGE,"E67")])]})]});}
            var Q5;
            Q5=makeQuery(id+"F8.boolean.opBoolean","INTERSECT",EDGE,{"disambiguationData":[OD(0.0)],"derivedFrom":[makeQuery(id+"F5.opExtrude","SWEPT_FACE",FACE,{"disambiguationData":[OSD([sQuery(id+"F4.wireOp",EDGE,"E30")])]}),makeQuery(id+"F8.opExtrude","SWEPT_FACE",FACE,{"disambiguationData":[OSD([sQuery(id+"F7.wireOp",EDGE,"E67")])]})]});
            fillet(context, id + "F14", {"entities" : qUnion([Q0, Q1, Q2, Q3, Q4, Q5]), "radius" : 3 * mm, "tangentPropagation" : true, "allowEdgeOverflow" : false});
        }
        {
            var Q0;
            Q0=makeQuery(id+"F1.opExtrude","CAP_EDGE",EDGE,{"disambiguationData":[OSD([sQuery(id+"F0.wireOp",EDGE,"E1.bottom")])],"isStart":false});
            fillet(context, id + "F15", {"entities" : qUnion([Q0]), "radius" : 2 * mm, "tangentPropagation" : true, "allowEdgeOverflow" : false});
        }
        {
            var Q0;
            {var subQ0=sQuery(id+"F0.wireOp",EDGE,"E21.filletArc");var subQ1=sQuery(id+"F0.wireOp",EDGE,"E7");var subQ2=sQuery(id+"F0.wireOp",EDGE,"E6");var subQ3=sQuery(id+"F0.wireOp",EDGE,"E5");var subQ4=sQuery(id+"F0.wireOp",EDGE,"E4");var subQ5=sQuery(id+"F0.wireOp",EDGE,"E22.filletArc");var subQ6=sQuery(id+"F0.wireOp",EDGE,"E1.bottom");var subQ7=sQuery(id+"F0.wireOp",EDGE,"E1.right");var subQ8=sQuery(id+"F0.wireOp",EDGE,"E1.top");var subQ9=sQuery(id+"F0.wireOp",EDGE,"E1.left");var subQ10=sQuery(id+"F0.wireOp",EDGE,"E23.filletArc");var subQ11=sQuery(id+"F0.wireOp",EDGE,"E24.filletArc");Q0=makeQuery(id+"F2.boolean.opBoolean","SPLIT",FACE,{"disambiguationData":[TD([makeQuery(id+"F1.opExtrude","SWEPT_FACE",FACE,{"disambiguationData":[OSD([subQ6])]})])],"derivedFrom":makeQuery(id+"F1.opExtrude","CAP_FACE",FACE,{"disambiguationData":[OSD([subQ6,subQ8,subQ9,subQ7,subQ4,subQ3,subQ2,subQ1,subQ0,subQ5,subQ10,subQ11])],"isStart":true})});}
            var sketch = newSketch(context, id + "F16", { "sketchPlane" : qUnion([Q0])});
            skLineSegment(sketch, "E79", {"start": v(0, 74.25) * mm, "end": v(0, 106.62) * mm, "construction": true});
            skCircle(sketch, "E80", {"center": v(0, 106.62) * mm, "radius": 6 * mm});
            skArc(sketch, "E81", {"start": v(14.62, 103.25) * mm, "mid": v(0.5, 121.61) * mm, "end": v(-14.81, 104.25) * mm});
            skLineSegment(sketch, "E82", {"start": v(-14.81, 104.25) * mm, "end": v(-14.81, 92.25) * mm});
            skLineSegment(sketch, "E83", {"start": v(-14.81, 92.25) * mm, "end": v(-32.81, 74.25) * mm});
            skLineSegment(sketch, "E84", {"start": v(14.62, 103.25) * mm, "end": v(14.62, 92.25) * mm});
            skLineSegment(sketch, "E85", {"start": v(14.62, 92.25) * mm, "end": v(32.62, 74.25) * mm});
            skLineSegment(sketch, "E86", {"start": v(-74.25, 0) * mm, "end": v(74.25, 0) * mm, "construction": true});
            skLineSegment(sketch, "E87.MirrorCS", {"start": v(14.81, 92.25) * mm, "end": v(32.81, 74.25) * mm});
            skLineSegment(sketch, "E88.MirrorCS", {"start": v(-14.62, 92.25) * mm, "end": v(-32.62, 74.25) * mm});
            skLineSegment(sketch, "E89.MirrorCS", {"start": v(-14.62, 103.25) * mm, "end": v(-14.62, 92.25) * mm});
            skLineSegment(sketch, "E90.MirrorCS", {"start": v(14.81, 104.25) * mm, "end": v(14.81, 92.25) * mm});
            skArc(sketch, "E91.MirrorCS", {"start": v(-14.62, 103.25) * mm, "mid": v(-0.5, 121.61) * mm, "end": v(14.81, 104.25) * mm});
            skLineSegment(sketch, "E92.MirrorCS", {"start": v(74.25, 0) * mm, "end": v(-74.25, 0) * mm, "construction": true});
            skLineSegment(sketch, "E93.MirrorCS", {"start": v(14.81, -104.25) * mm, "end": v(14.81, -92.25) * mm});
            skLineSegment(sketch, "E94.MirrorCS", {"start": v(14.62, -103.25) * mm, "end": v(14.62, -92.25) * mm});
            skLineSegment(sketch, "E95.MirrorCS", {"start": v(-14.62, -103.25) * mm, "end": v(-14.62, -92.25) * mm});
            skLineSegment(sketch, "E96.MirrorCS", {"start": v(-14.81, -104.25) * mm, "end": v(-14.81, -92.25) * mm});
            skCircle(sketch, "E97.MirrorC", {"center": v(0, -106.62) * mm, "radius": 6 * mm});
            skLineSegment(sketch, "E98.MirrorCS", {"start": v(14.81, -92.25) * mm, "end": v(32.81, -74.25) * mm});
            skLineSegment(sketch, "E99.MirrorCS", {"start": v(14.62, -92.25) * mm, "end": v(32.62, -74.25) * mm});
            skLineSegment(sketch, "E100.MirrorCS", {"start": v(-14.62, -92.25) * mm, "end": v(-32.62, -74.25) * mm});
            skArc(sketch, "E101.MirrorCS", {"start": v(-14.62, -103.25) * mm, "mid": v(-0.5, -121.61) * mm, "end": v(14.81, -104.25) * mm});
            skArc(sketch, "E102.MirrorCS", {"start": v(14.62, -103.25) * mm, "mid": v(0.5, -121.61) * mm, "end": v(-14.81, -104.25) * mm});
            skLineSegment(sketch, "E103.MirrorCS", {"start": v(-14.81, -92.25) * mm, "end": v(-32.81, -74.25) * mm});
            skLineSegment(sketch, "E104.MirrorCS", {"start": v(0, -74.25) * mm, "end": v(0, -106.62) * mm, "construction": true});
            skSolve(sketch);
        }
        {
            var Q0;
            Q0=makeQuery(id+"F16.imprint","IMPRINT",FACE,{"disambiguationData":[TD([[makeQuery(id+"F16.imprint","IMPRINT",EDGE,{"derivedFrom":sQuery(id+"F16.wireOp",EDGE,"E84")}),-1.0]])]});
            var Q1;
            Q1=makeQuery(id+"F16.imprint","IMPRINT",FACE,{"disambiguationData":[TD([[makeQuery(id+"F16.imprint","IMPRINT",EDGE,{"derivedFrom":makeQuery(id+"F1.opExtrude","CAP_EDGE",EDGE,{"disambiguationData":[OSD([sQuery(id+"F0.wireOp",EDGE,"E1.left")])],"isStart":true})}),-1.0]])]});
            var Q2;
            {var subQ2=sQuery(id+"F16.wireOp",EDGE,"E94.MirrorCS");Q2=makeQuery(id+"F16.imprint","IMPRINT",FACE,{"disambiguationData":[TD([[makeQuery(id+"F16.imprint","IMPRINT",EDGE,{"derivedFrom":subQ2}),1.0]])]});}
            var Q3;
            Q3=makeQuery(id+"F2.opExtrude","CAP_FACE",FACE,{"disambiguationData":[OSD([sQuery(id+"F0.wireOp",EDGE,"E12"),sQuery(id+"F0.wireOp",EDGE,"E13"),sQuery(id+"F0.wireOp",EDGE,"E14"),sQuery(id+"F0.wireOp",EDGE,"E15"),sQuery(id+"F0.wireOp",EDGE,"E17.filletArc"),sQuery(id+"F0.wireOp",EDGE,"E18.filletArc"),sQuery(id+"F0.wireOp",EDGE,"E19.filletArc"),sQuery(id+"F0.wireOp",EDGE,"E20.filletArc"),sQuery(id+"F0.wireOp",EDGE,"E25.0"),sQuery(id+"F0.wireOp",EDGE,"E25.1"),sQuery(id+"F0.wireOp",EDGE,"E25.2"),sQuery(id+"F0.wireOp",EDGE,"E25.3"),sQuery(id+"F0.wireOp",EDGE,"E25.4"),sQuery(id+"F0.wireOp",EDGE,"E25.5"),sQuery(id+"F0.wireOp",EDGE,"E25.6"),sQuery(id+"F0.wireOp",EDGE,"E25.7")])],"isStart":false});
            extrude(context, id + "F17", {"entities" : qUnion([Q0, Q1, Q2]), "endBound" : BoundingType.UP_TO_SURFACE, "endBoundEntityFace" : qUnion([Q3]), "depth" : 25 * mm});
        }
    });
